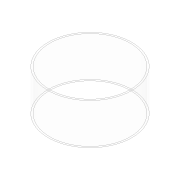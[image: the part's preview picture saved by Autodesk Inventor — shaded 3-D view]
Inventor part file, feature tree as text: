
AUTODESK INVENTOR PART (.ipt)
format: ipt  version: 2018 (Build 220112000, 112)  size: 81,408 bytes
history: native  units: mm
features: extrude x1, sketch x1
ambient origin geometry x8: Origin, YZ Plane, XZ Plane, XY Plane, X Axis, Y Axis, Z Axis, Center Point
bodies: Solid1 (feature_tree)
feature tree (2):
  extrude  "Extrusion1"  [1 undecoded]
  sketch  "Sketch1"  dims[d0=76.2mm d1=79.375mm d2=38.75mm d3=0.0mm]
note: 1 required parameter value undecoded (feature->parameter linkage not recoverable at this tier; creation-order binding heuristic only, values carry confidence <= 0.55)
